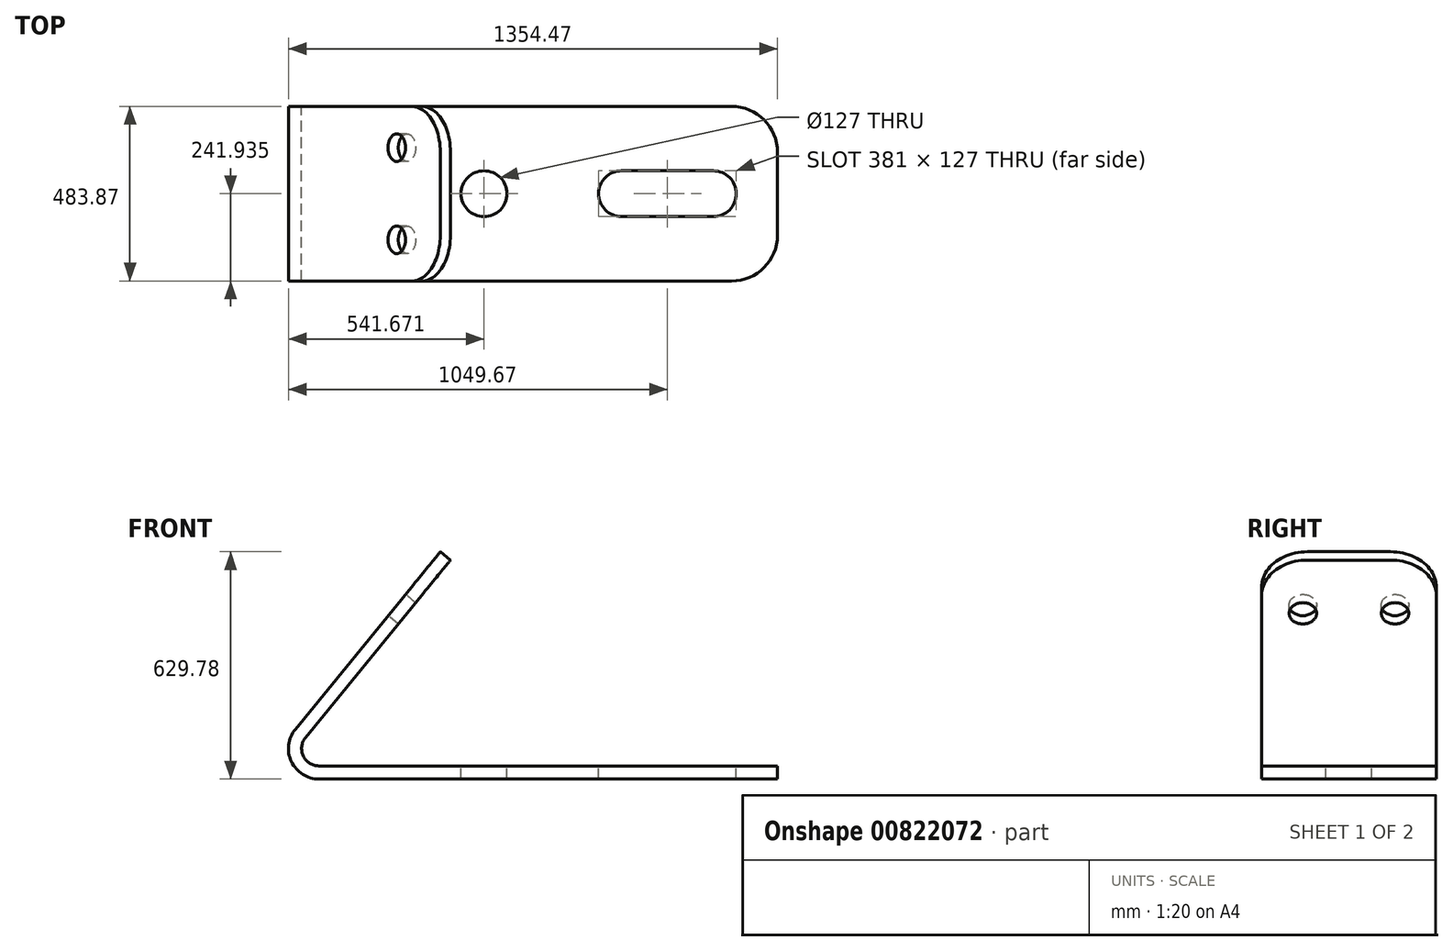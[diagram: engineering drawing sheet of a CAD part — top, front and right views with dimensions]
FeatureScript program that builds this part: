
annotation { "Feature Type Name" : "Feature", "Feature Type Description" : "" }
export const myFeature = defineFeature(function(context is Context, id is Id, definition is map)
    precondition{}
    {
        {
            var Q0;
            Q0=qCreatedBy(makeId("Front.planeOp"),FACE);
            var sketch = newSketch(context, id + "F0", { "sketchPlane" : qUnion([Q0])});
            skLineSegment(sketch, "E0", {"start": v(112.58, 137.9) * mm, "end": v(514.18, 629.78) * mm});
            skLineSegment(sketch, "E1", {"start": v(178.02, 0) * mm, "end": v(1448.02, 0) * mm});
            skPoint(sketch, "E2.visualSharp", {"position": v(0, 0) * mm});
            skArc(sketch, "E2.filletArc", {"start": v(112.58, 137.9) * mm, "mid": v(101.7, 48.26) * mm, "end": v(178.02, 0) * mm});
            skLineSegment(sketch, "E3", {"start": v(514.18, 629.78) * mm, "end": v(542.43, 606.71) * mm});
            skLineSegment(sketch, "E4", {"start": v(542.43, 606.71) * mm, "end": v(140.84, 114.83) * mm});
            skLineSegment(sketch, "E5", {"start": v(1448.02, 0) * mm, "end": v(1448.02, 36.48) * mm});
            skLineSegment(sketch, "E6", {"start": v(1448.02, 36.48) * mm, "end": v(178.02, 36.48) * mm});
            skArc(sketch, "E7", {"start": v(140.84, 114.83) * mm, "mid": v(134.66, 63.9) * mm, "end": v(178.02, 36.48) * mm});
            skPoint(sketch, "E8.orphan", {"position": v(101.7, 48.26) * mm});
            skPoint(sketch, "E9.start.orphan", {"position": v(145.3, 68.95) * mm});
            skSolve(sketch);
        }
        {
            var Q0;
            Q0=makeQuery(id+"F0.imprint","IMPRINT",FACE,{"disambiguationData":[TD([[makeQuery(id+"F0.imprint","IMPRINT",EDGE,{"derivedFrom":sQuery(id+"F0.wireOp",EDGE,"E0")}),-1.0]])]});
            extrude(context, id + "F1", {"entities" : qUnion([Q0]), "depth" : 483.87 * mm, "offsetDistance" : 25.4 * mm});
        }
        {
            var Q0;
            Q0=makeQuery(id+"F1.opExtrude","CAP_EDGE",EDGE,{"disambiguationData":[OSD([sQuery(id+"F0.wireOp",EDGE,"E5")])],"isStart":false});
            var Q1;
            Q1=makeQuery(id+"F1.opExtrude","CAP_EDGE",EDGE,{"disambiguationData":[OSD([sQuery(id+"F0.wireOp",EDGE,"E5")])],"isStart":true});
            var Q2;
            Q2=makeQuery(id+"F1.opExtrude","CAP_EDGE",EDGE,{"disambiguationData":[OSD([sQuery(id+"F0.wireOp",EDGE,"E3")])],"isStart":false});
            var Q3;
            Q3=makeQuery(id+"F1.opExtrude","CAP_EDGE",EDGE,{"disambiguationData":[OSD([sQuery(id+"F0.wireOp",EDGE,"E3")])],"isStart":true});
            fillet(context, id + "F2", {"entities" : qUnion([Q0, Q1, Q2, Q3]), "radius" : 127 * mm, "tangentPropagation" : true, "allowEdgeOverflow" : false});
        }
        {
            var Q0;
            Q0=makeQuery(id+"F1.opExtrude","SWEPT_FACE",FACE,{"disambiguationData":[OSD([sQuery(id+"F0.wireOp",EDGE,"E0")])]});
            var sketch = newSketch(context, id + "F3", { "sketchPlane" : qUnion([Q0])});
            skPoint(sketch, "E10.end.orphan", {"position": v(369.57, 178.02) * mm});
            skPoint(sketch, "E11.orphan", {"position": v(241.94, 178.02) * mm});
            skPoint(sketch, "E12.start.orphan", {"position": v(241.94, 813.02) * mm});
            skCircle(sketch, "E13", {"center": v(114.3, 622.52) * mm, "radius": 38.1 * mm});
            skCircle(sketch, "E14", {"center": v(369.57, 622.52) * mm, "radius": 38.1 * mm});
            skSolve(sketch);
        }
        {
            var Q0;
            Q0=makeQuery(id+"F3.imprint","IMPRINT",FACE,{"disambiguationData":[TD([[makeQuery(id+"F3.imprint","IMPRINT",EDGE,{"derivedFrom":sQuery(id+"F3.wireOp",EDGE,"E13")}),1.0]])]});
            var Q1;
            Q1=makeQuery(id+"F3.imprint","IMPRINT",FACE,{"disambiguationData":[TD([[makeQuery(id+"F3.imprint","IMPRINT",EDGE,{"derivedFrom":sQuery(id+"F3.wireOp",EDGE,"E14")}),1.0]])]});
            extrude(context, id + "F4", {"entities" : qUnion([Q0, Q1]), "operationType" : NewBodyOperationType.REMOVE, "oppositeDirection" : true, "depth" : 99.06 * mm, "offsetDistance" : 25.4 * mm});
        }
        {
            var Q0;
            Q0=makeQuery(id+"F1.opExtrude","SWEPT_FACE",FACE,{"disambiguationData":[OSD([sQuery(id+"F0.wireOp",EDGE,"E6")])]});
            var sketch = newSketch(context, id + "F5", { "sketchPlane" : qUnion([Q0])});
            skCircle(sketch, "E15", {"center": v(635.22, -241.94) * mm, "radius": 63.5 * mm});
            skLineSegment(sketch, "E16", {"start": v(1270.22, -178.43) * mm, "end": v(1016.22, -178.43) * mm});
            skLineSegment(sketch, "E17", {"start": v(1016.22, -305.44) * mm, "end": v(1270.22, -305.44) * mm});
            skArc(sketch, "E18", {"start": v(1270.22, -305.44) * mm, "mid": v(1333.72, -241.94) * mm, "end": v(1270.22, -178.44) * mm});
            skPoint(sketch, "E19.orphan", {"position": v(1333.72, -305.44) * mm});
            skPoint(sketch, "E20.end.orphan", {"position": v(1270.22, -178.43) * mm});
            skArc(sketch, "E21", {"start": v(1016.22, -305.44) * mm, "mid": v(952.72, -241.94) * mm, "end": v(1016.22, -178.44) * mm});
            skPoint(sketch, "E22.orphan", {"position": v(952.72, -305.44) * mm});
            skPoint(sketch, "E23.orphan", {"position": v(1016.22, -178.43) * mm});
            skPoint(sketch, "E24.start.orphan", {"position": v(1448.02, -241.94) * mm});
            skPoint(sketch, "E25.trimOffspring.end.orphan", {"position": v(178.02, -241.94) * mm});
            skSolve(sketch);
        }
        {
            var Q0;
            Q0=makeQuery(id+"F5.imprint","IMPRINT",FACE,{"disambiguationData":[TD([[makeQuery(id+"F5.imprint","IMPRINT",EDGE,{"derivedFrom":sQuery(id+"F5.wireOp",EDGE,"E15")}),1.0]])]});
            var Q1;
            Q1=makeQuery(id+"F5.imprint","IMPRINT",FACE,{"disambiguationData":[TD([[makeQuery(id+"F5.imprint","IMPRINT",EDGE,{"derivedFrom":sQuery(id+"F5.wireOp",EDGE,"E16")}),1.0]])]});
            extrude(context, id + "F6", {"entities" : qUnion([Q0, Q1]), "operationType" : NewBodyOperationType.REMOVE, "oppositeDirection" : true, "depth" : 360.68 * mm, "offsetDistance" : 25.4 * mm});
        }
    });
